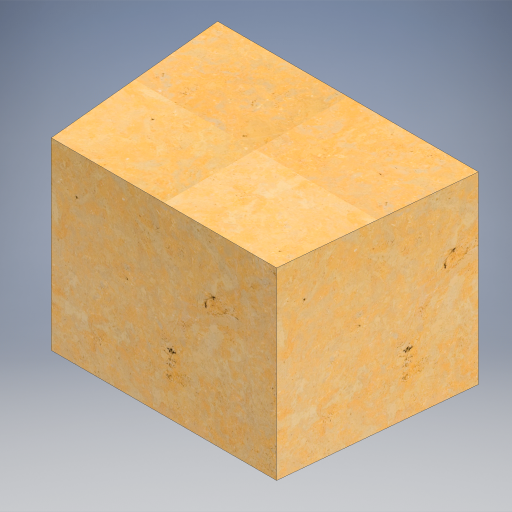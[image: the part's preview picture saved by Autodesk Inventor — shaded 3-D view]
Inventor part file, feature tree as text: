
AUTODESK INVENTOR PART (.ipt)
format: ipt  version: 2023 (Build 270158030, 158C)  size: 546,816 bytes
history: native  units: in
note: dims shown in document units (in); Inventor stores cm internally (conversion verified against a paired STEP export)
features: extrude x1, sketch x1
ambient origin geometry x8: Origin, YZ Plane, XZ Plane, XY Plane, X Axis, Y Axis, Z Axis, Center Point
bodies: Solid1 (feature_tree)
feature tree (2):
  extrude  "Extrusion1"  Depth=24.0in
  sketch  "Sketch1"  dims[d0=34.0in d1=24.0in d2=0.0756in d3=24.0in d4=0.0in d5=24.0in]
